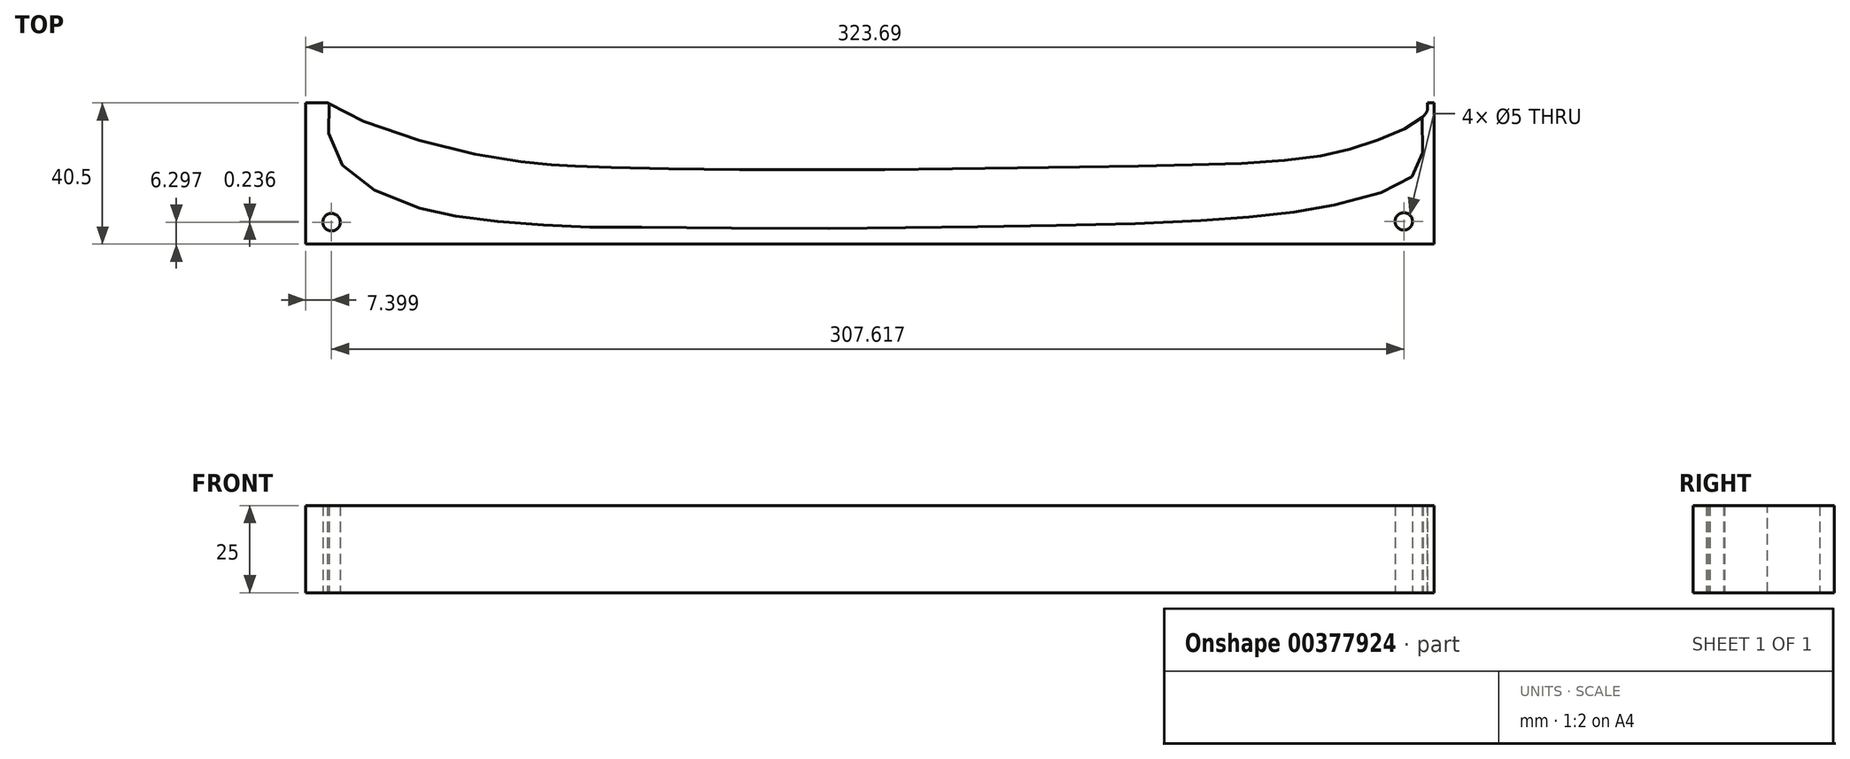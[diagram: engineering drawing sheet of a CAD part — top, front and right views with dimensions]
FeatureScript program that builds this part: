
annotation { "Feature Type Name" : "Feature", "Feature Type Description" : "" }
export const myFeature = defineFeature(function(context is Context, id is Id, definition is map)
    precondition{}
    {
        {
            var Q0;
            Q0=qCreatedBy(makeId("Top.planeOp"),FACE);
            var sketch = newSketch(context, id + "F0", { "sketchPlane" : qUnion([Q0])});
            skLineSegment(sketch, "E0", {"start": v(-105.58, -2.36) * mm, "end": v(94.42, -2.36) * mm});
            skFitSpline(sketch, "E1", {"points": [v(-140.23, 64.32) * mm, v(-140.4, 60.24) * mm, v(-139.64, 58.6) * mm, v(-112.66, 47.57) * mm, v(-81.66, 41.43) * mm, v(-72.59, 40.66) * mm, v(-61.6, 40.13) * mm, v(-8.27, 39.44) * mm, v(52.34, 39.87) * mm, v(98.53, 40.64) * mm, v(129.33, 41.67) * mm, v(146.78, 43.72) * mm, v(157.13, 46.46) * mm, v(167.88, 50.5) * mm, v(173.36, 53.74) * mm, v(175.5, 56.1) * mm, v(175.66, 58.6) * mm], "startDerivative": vector(-23.45, -234.45) * mm, "endDerivative": vector(-13.94, 158.91) * mm});
            skFitSpline(sketch, "E2", {"points": [v(173.87, 58.6) * mm, v(174.3, 51.5) * mm, v(174.3, 43.72) * mm, v(173, 39.37) * mm, v(169.33, 36.09) * mm, v(161.17, 32.42) * mm, v(146.59, 28.85) * mm, v(136.72, 27.18) * mm, v(123.82, 25.79) * mm, v(108.68, 24.72) * mm, v(75.88, 23.58) * mm, v(37.5, 22.96) * mm, v(2.03, 22.58) * mm, v(-51.91, 22.96) * mm, v(-66.79, 23.04) * mm, v(-81.1, 23.8) * mm, v(-93.72, 24.87) * mm, v(-104.4, 26.4) * mm, v(-112.71, 28.23) * mm, v(-126.45, 33.57) * mm, v(-134.84, 39.9) * mm, v(-138.73, 46.84) * mm, v(-139.87, 53.1) * mm, v(-139.28, 58.6) * mm], "startDerivative": vector(14.42, -222.27) * mm, "endDerivative": vector(49.5, 249.47) * mm});
            skLineSegment(sketch, "E3.bottom", {"start": v(-146.11, 58.6) * mm, "end": v(177.58, 58.6) * mm});
            skLineSegment(sketch, "E3.top", {"start": v(-146.11, 18.09) * mm, "end": v(177.58, 18.09) * mm});
            skLineSegment(sketch, "E3.left", {"start": v(-146.11, 58.6) * mm, "end": v(-146.11, 18.09) * mm});
            skLineSegment(sketch, "E3.right", {"start": v(177.58, 58.6) * mm, "end": v(177.58, 18.09) * mm});
            skCircle(sketch, "E4", {"center": v(-138.71, 24.39) * mm, "radius": 2.5 * mm});
            skCircle(sketch, "E5", {"center": v(168.9, 24.62) * mm, "radius": 2.5 * mm});
            skSolve(sketch);
        }
        {
            var Q0;
            Q0=makeQuery(id+"F0.imprint","IMPRINT",FACE,{"disambiguationData":[TD([[makeQuery(id+"F0.imprint","IMPRINT",EDGE,{"derivedFrom":sQuery(id+"F0.wireOp",EDGE,"E3.top")}),1.0]])]});
            var Q1;
            {var subQ0=sQuery(id+"F0.wireOp",EDGE,"E2");var subQ1=sQuery(id+"F0.wireOp",EDGE,"E1");var subQ2=makeQuery(id+"F0.imprint","INTERSECT",VERTEX,{"disambiguationData":[OD(0.0)],"derivedFrom":[subQ1,subQ0]});Q1=makeQuery(id+"F0.imprint","IMPRINT",FACE,{"disambiguationData":[TD([[makeQuery(id+"F0.imprint","IMPRINT",EDGE,{"disambiguationData":[TD([[subQ2,-1.0]])],"derivedFrom":subQ1}),-1.0]])]});}
            extrude(context, id + "F1", {"entities" : qUnion([Q0, Q1]), "depth" : 25 * mm});
        }
        {
            var Q0;
            Q0=makeQuery(id+"F0.imprint","IMPRINT",FACE,{"disambiguationData":[TD([[makeQuery(id+"F0.imprint","IMPRINT",EDGE,{"derivedFrom":sQuery(id+"F0.wireOp",EDGE,"E3.top")}),1.0]])]});
            extrude(context, id + "F2", {"entities" : qUnion([Q0]), "depth" : 25 * mm});
        }
    });
